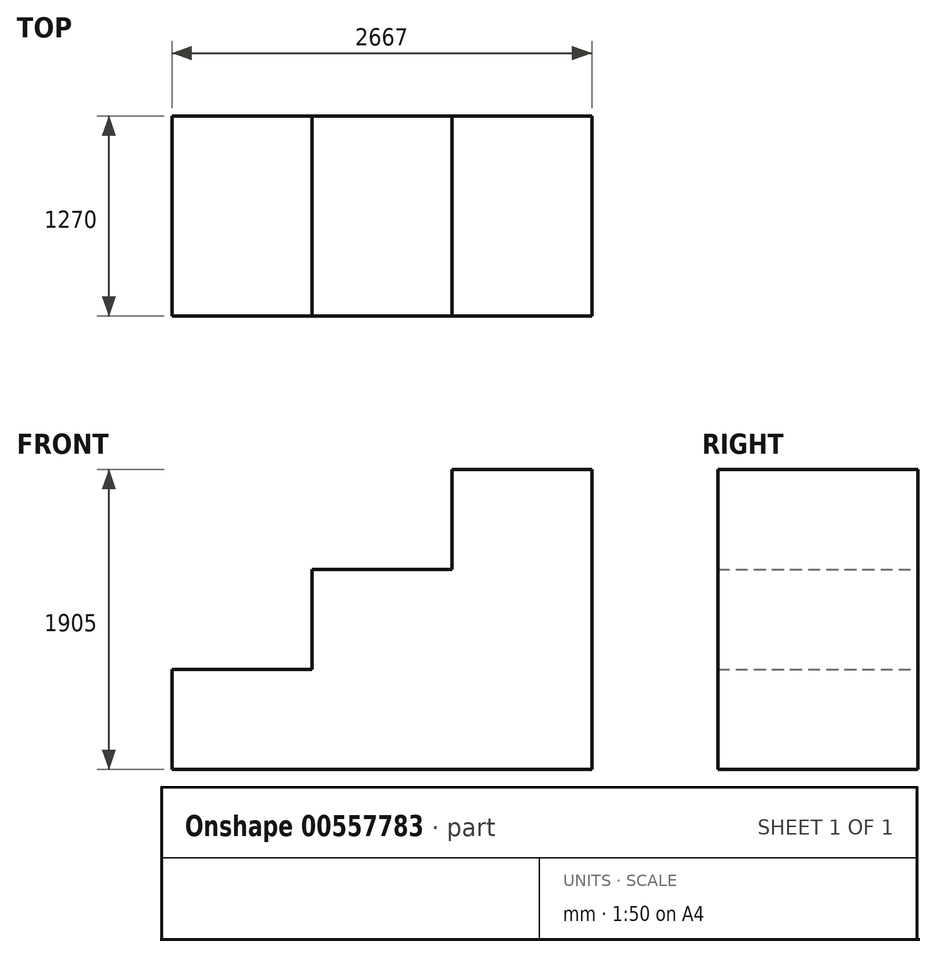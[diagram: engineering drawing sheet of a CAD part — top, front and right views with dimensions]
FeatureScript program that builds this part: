
annotation { "Feature Type Name" : "Feature", "Feature Type Description" : "" }
export const myFeature = defineFeature(function(context is Context, id is Id, definition is map)
    precondition{}
    {
        {
            var Q0;
            Q0=qCreatedBy(makeId("Front.planeOp"),FACE);
            var sketch = newSketch(context, id + "F0", { "sketchPlane" : qUnion([Q0])});
            skLineSegment(sketch, "E0", {"start": v(-123.15, -30.6) * mm, "end": v(2543.85, -30.6) * mm});
            skLineSegment(sketch, "E1", {"start": v(2543.85, -30.6) * mm, "end": v(2543.85, 1874.4) * mm});
            skLineSegment(sketch, "E2", {"start": v(2543.85, 1874.4) * mm, "end": v(1654.85, 1874.4) * mm});
            skLineSegment(sketch, "E3", {"start": v(1654.85, 1874.4) * mm, "end": v(1654.85, 1239.4) * mm});
            skLineSegment(sketch, "E4", {"start": v(1654.85, 1239.4) * mm, "end": v(765.85, 1239.4) * mm});
            skLineSegment(sketch, "E5", {"start": v(765.85, 1239.4) * mm, "end": v(765.85, 604.4) * mm});
            skLineSegment(sketch, "E6", {"start": v(765.85, 604.4) * mm, "end": v(-123.15, 604.4) * mm});
            skLineSegment(sketch, "E7", {"start": v(-123.15, 604.4) * mm, "end": v(-123.15, -30.6) * mm});
            skSolve(sketch);
        }
        {
            var Q0;
            Q0=makeQuery(id+"F0.imprint","IMPRINT",FACE,{"disambiguationData":[TD([[makeQuery(id+"F0.imprint","IMPRINT",EDGE,{"derivedFrom":sQuery(id+"F0.wireOp",EDGE,"E0")}),1.0]])]});
            extrude(context, id + "F1", {"entities" : qUnion([Q0]), "depth" : 1270 * mm, "offsetDistance" : 25.4 * mm});
        }
    });
